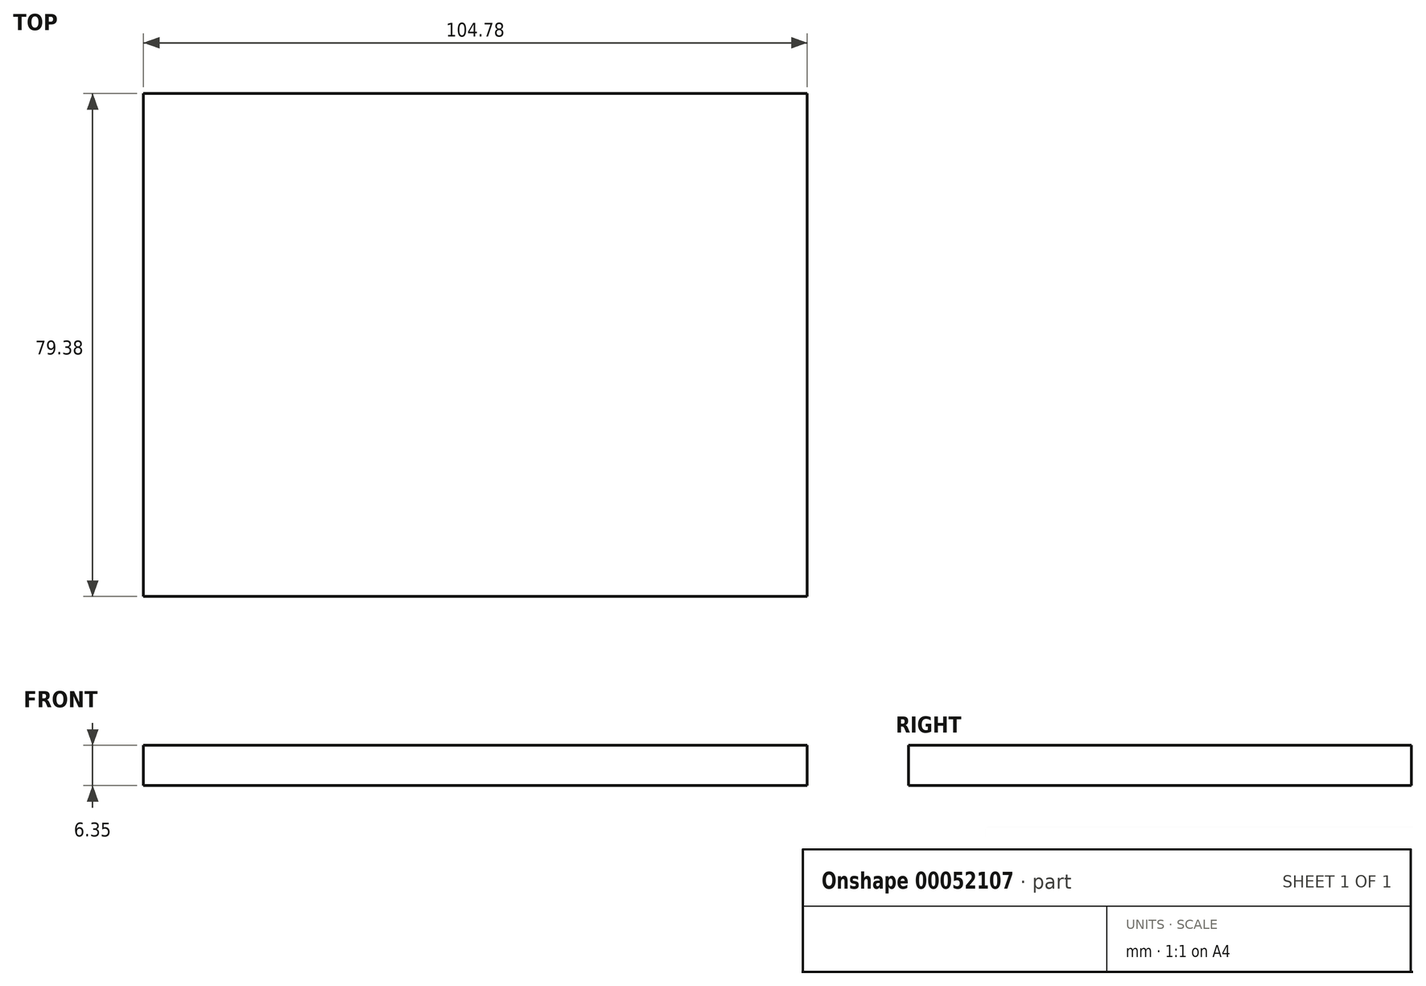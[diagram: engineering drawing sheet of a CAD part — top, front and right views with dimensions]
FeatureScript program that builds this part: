
annotation { "Feature Type Name" : "Feature", "Feature Type Description" : "" }
export const myFeature = defineFeature(function(context is Context, id is Id, definition is map)
    precondition{}
    {
        {
            var Q0;
            Q0=qCreatedBy(makeId("Top.planeOp"),FACE);
            var sketch = newSketch(context, id + "F0", { "sketchPlane" : qUnion([Q0])});
            skLineSegment(sketch, "E0.rect.bottom", {"start": v(52.39, -39.69) * mm, "end": v(-52.39, -39.69) * mm});
            skLineSegment(sketch, "E0.rect.top", {"start": v(52.39, 39.69) * mm, "end": v(-52.39, 39.69) * mm});
            skLineSegment(sketch, "E0.rect.left", {"start": v(52.39, -39.69) * mm, "end": v(52.39, 39.69) * mm});
            skLineSegment(sketch, "E0.rect.right", {"start": v(-52.39, -39.69) * mm, "end": v(-52.39, 39.69) * mm});
            skPoint(sketch, "E0.rect.middle", {"position": v(0, 0) * mm});
            skSolve(sketch);
        }
        {
            var Q0;
            Q0 = qSketchRegion(id + "F0", true);
            extrude(context, id + "F1", {"entities" : qUnion([Q0]), "depth" : 6.35 * mm});
        }
    });
